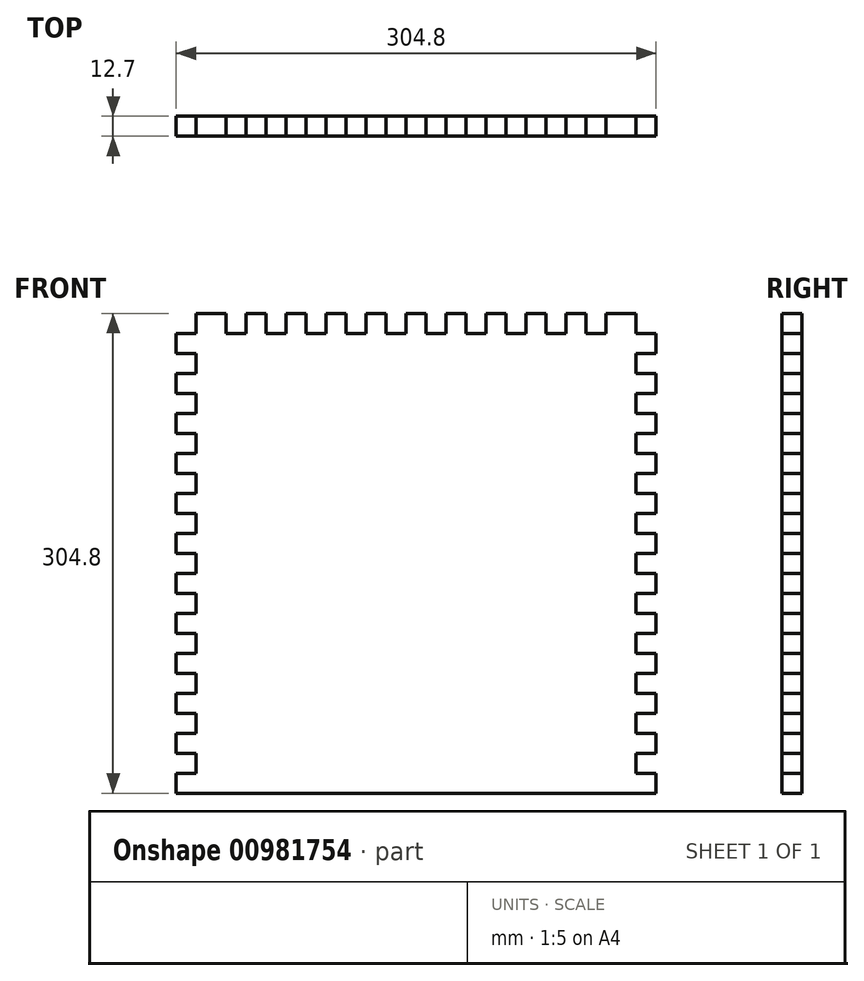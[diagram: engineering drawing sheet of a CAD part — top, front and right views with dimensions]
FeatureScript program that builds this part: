
annotation { "Feature Type Name" : "Feature", "Feature Type Description" : "" }
export const myFeature = defineFeature(function(context is Context, id is Id, definition is map)
    precondition{}
    {
        {
            var Q0;
            Q0=qCreatedBy(makeId("Front.planeOp"),FACE);
            var sketch = newSketch(context, id + "F0", { "sketchPlane" : qUnion([Q0])});
            skLineSegment(sketch, "E0.top", {"start": v(139.7, -142.06) * mm, "end": v(-139.7, -142.06) * mm});
            skPoint(sketch, "E0.middle", {"position": v(0, -2.36) * mm});
            skLineSegment(sketch, "E1", {"start": v(-139.7, -142.06) * mm, "end": v(-152.4, -142.06) * mm});
            skLineSegment(sketch, "E2", {"start": v(-152.4, -142.06) * mm, "end": v(-152.4, -129.36) * mm});
            skLineSegment(sketch, "E3", {"start": v(-152.4, -129.36) * mm, "end": v(-139.7, -129.36) * mm});
            skLineSegment(sketch, "E4", {"start": v(-139.7, -129.36) * mm, "end": v(-139.7, -116.66) * mm});
            skLineSegment(sketch, "E5.0.1.0", {"start": v(-152.4, -103.96) * mm, "end": v(-139.7, -103.96) * mm});
            skLineSegment(sketch, "E5.0.1.1", {"start": v(-139.7, -116.66) * mm, "end": v(-152.4, -116.66) * mm});
            skLineSegment(sketch, "E5.0.1.2", {"start": v(-152.4, -116.66) * mm, "end": v(-152.4, -103.96) * mm});
            skLineSegment(sketch, "E5.0.1.3", {"start": v(-139.7, -103.96) * mm, "end": v(-139.7, -91.26) * mm});
            skLineSegment(sketch, "E5.0.2.0", {"start": v(-152.4, -78.56) * mm, "end": v(-139.7, -78.56) * mm});
            skLineSegment(sketch, "E5.0.2.1", {"start": v(-139.7, -91.26) * mm, "end": v(-152.4, -91.26) * mm});
            skLineSegment(sketch, "E5.0.2.2", {"start": v(-152.4, -91.26) * mm, "end": v(-152.4, -78.56) * mm});
            skLineSegment(sketch, "E5.0.2.3", {"start": v(-139.7, -78.56) * mm, "end": v(-139.7, -65.86) * mm});
            skLineSegment(sketch, "E5.0.3.0", {"start": v(-152.4, -53.16) * mm, "end": v(-139.7, -53.16) * mm});
            skLineSegment(sketch, "E5.0.3.1", {"start": v(-139.7, -65.86) * mm, "end": v(-152.4, -65.86) * mm});
            skLineSegment(sketch, "E5.0.3.2", {"start": v(-152.4, -65.86) * mm, "end": v(-152.4, -53.16) * mm});
            skLineSegment(sketch, "E5.0.3.3", {"start": v(-139.7, -53.16) * mm, "end": v(-139.7, -40.46) * mm});
            skLineSegment(sketch, "E5.0.4.0", {"start": v(-152.4, -27.76) * mm, "end": v(-139.7, -27.76) * mm});
            skLineSegment(sketch, "E5.0.4.1", {"start": v(-139.7, -40.46) * mm, "end": v(-152.4, -40.46) * mm});
            skLineSegment(sketch, "E5.0.4.2", {"start": v(-152.4, -40.46) * mm, "end": v(-152.4, -27.76) * mm});
            skLineSegment(sketch, "E5.0.4.3", {"start": v(-139.7, -27.76) * mm, "end": v(-139.7, -15.06) * mm});
            skLineSegment(sketch, "E5.0.5.0", {"start": v(-152.4, -2.36) * mm, "end": v(-139.7, -2.36) * mm});
            skLineSegment(sketch, "E5.0.5.1", {"start": v(-139.7, -15.06) * mm, "end": v(-152.4, -15.06) * mm});
            skLineSegment(sketch, "E5.0.5.2", {"start": v(-152.4, -15.06) * mm, "end": v(-152.4, -2.36) * mm});
            skLineSegment(sketch, "E5.0.5.3", {"start": v(-139.7, -2.36) * mm, "end": v(-139.7, 10.34) * mm});
            skLineSegment(sketch, "E5.0.6.0", {"start": v(-152.4, 23.04) * mm, "end": v(-139.7, 23.04) * mm});
            skLineSegment(sketch, "E5.0.6.1", {"start": v(-139.7, 10.34) * mm, "end": v(-152.4, 10.34) * mm});
            skLineSegment(sketch, "E5.0.6.2", {"start": v(-152.4, 10.34) * mm, "end": v(-152.4, 23.04) * mm});
            skLineSegment(sketch, "E5.0.6.3", {"start": v(-139.7, 23.04) * mm, "end": v(-139.7, 35.74) * mm});
            skLineSegment(sketch, "E5.0.7.0", {"start": v(-152.4, 48.44) * mm, "end": v(-139.7, 48.44) * mm});
            skLineSegment(sketch, "E5.0.7.1", {"start": v(-139.7, 35.74) * mm, "end": v(-152.4, 35.74) * mm});
            skLineSegment(sketch, "E5.0.7.2", {"start": v(-152.4, 35.74) * mm, "end": v(-152.4, 48.44) * mm});
            skLineSegment(sketch, "E5.0.7.3", {"start": v(-139.7, 48.44) * mm, "end": v(-139.7, 61.14) * mm});
            skLineSegment(sketch, "E5.0.8.0", {"start": v(-152.4, 73.84) * mm, "end": v(-139.7, 73.84) * mm});
            skLineSegment(sketch, "E5.0.8.1", {"start": v(-139.7, 61.14) * mm, "end": v(-152.4, 61.14) * mm});
            skLineSegment(sketch, "E5.0.8.2", {"start": v(-152.4, 61.14) * mm, "end": v(-152.4, 73.84) * mm});
            skLineSegment(sketch, "E5.0.8.3", {"start": v(-139.7, 73.84) * mm, "end": v(-139.7, 86.54) * mm});
            skLineSegment(sketch, "E5.0.9.0", {"start": v(-152.4, 99.24) * mm, "end": v(-139.7, 99.24) * mm});
            skLineSegment(sketch, "E5.0.9.1", {"start": v(-139.7, 86.54) * mm, "end": v(-152.4, 86.54) * mm});
            skLineSegment(sketch, "E5.0.9.2", {"start": v(-152.4, 86.54) * mm, "end": v(-152.4, 99.24) * mm});
            skLineSegment(sketch, "E5.0.9.3", {"start": v(-139.7, 99.24) * mm, "end": v(-139.7, 111.94) * mm});
            skLineSegment(sketch, "E5.0.10.0", {"start": v(-152.4, 124.64) * mm, "end": v(-139.7, 124.64) * mm});
            skLineSegment(sketch, "E5.0.10.1", {"start": v(-139.7, 111.94) * mm, "end": v(-152.4, 111.94) * mm});
            skLineSegment(sketch, "E5.0.10.2", {"start": v(-152.4, 111.94) * mm, "end": v(-152.4, 124.64) * mm});
            skLineSegment(sketch, "E5.0.10.3", {"start": v(-139.7, 124.64) * mm, "end": v(-139.7, 137.34) * mm});
            skLineSegment(sketch, "E5.direction1", {"start": v(-152.4, -142.06) * mm, "end": v(-127, -142.06) * mm, "construction": true});
            skLineSegment(sketch, "E5.direction2", {"start": v(-152.4, -142.06) * mm, "end": v(-152.4, -116.66) * mm, "construction": true});
            skLineSegment(sketch, "E6.MirrorCS", {"start": v(139.7, 48.44) * mm, "end": v(139.7, 61.14) * mm});
            skLineSegment(sketch, "E7.MirrorCS", {"start": v(139.7, -27.76) * mm, "end": v(139.7, -15.06) * mm});
            skLineSegment(sketch, "E8.MirrorCS", {"start": v(152.4, 111.94) * mm, "end": v(152.4, 124.64) * mm});
            skLineSegment(sketch, "E9.MirrorCS", {"start": v(139.7, 124.64) * mm, "end": v(139.7, 137.34) * mm});
            skLineSegment(sketch, "E10.MirrorCS", {"start": v(139.7, -129.36) * mm, "end": v(139.7, -116.66) * mm});
            skLineSegment(sketch, "E11.MirrorCS", {"start": v(152.4, 10.34) * mm, "end": v(152.4, 23.04) * mm});
            skLineSegment(sketch, "E12.MirrorCS", {"start": v(139.7, -103.96) * mm, "end": v(139.7, -91.26) * mm});
            skLineSegment(sketch, "E13.MirrorCS", {"start": v(152.4, -15.06) * mm, "end": v(152.4, -2.36) * mm});
            skLineSegment(sketch, "E14.MirrorCS", {"start": v(152.4, -142.06) * mm, "end": v(152.4, -129.36) * mm});
            skLineSegment(sketch, "E15.MirrorCS", {"start": v(152.4, -91.26) * mm, "end": v(152.4, -78.56) * mm});
            skLineSegment(sketch, "E16.MirrorCS", {"start": v(152.4, -65.86) * mm, "end": v(152.4, -53.16) * mm});
            skLineSegment(sketch, "E17.MirrorCS", {"start": v(152.4, 35.74) * mm, "end": v(152.4, 48.44) * mm});
            skLineSegment(sketch, "E18.MirrorCS", {"start": v(139.7, 73.84) * mm, "end": v(139.7, 86.54) * mm});
            skLineSegment(sketch, "E19.MirrorCS", {"start": v(139.7, -53.16) * mm, "end": v(139.7, -40.46) * mm});
            skLineSegment(sketch, "E20.MirrorCS", {"start": v(152.4, 86.54) * mm, "end": v(152.4, 99.24) * mm});
            skLineSegment(sketch, "E21.MirrorCS", {"start": v(139.7, -116.66) * mm, "end": v(152.4, -116.66) * mm});
            skLineSegment(sketch, "E22.MirrorCS", {"start": v(152.4, 61.14) * mm, "end": v(152.4, 73.84) * mm});
            skLineSegment(sketch, "E23.MirrorCS", {"start": v(139.7, -78.56) * mm, "end": v(139.7, -65.86) * mm});
            skLineSegment(sketch, "E24.MirrorCS", {"start": v(152.4, 48.44) * mm, "end": v(139.7, 48.44) * mm});
            skLineSegment(sketch, "E25.MirrorCS", {"start": v(152.4, -53.16) * mm, "end": v(139.7, -53.16) * mm});
            skLineSegment(sketch, "E26.MirrorCS", {"start": v(139.7, 99.24) * mm, "end": v(139.7, 111.94) * mm});
            skLineSegment(sketch, "E27.MirrorCS", {"start": v(139.7, -142.06) * mm, "end": v(152.4, -142.06) * mm});
            skLineSegment(sketch, "E28.MirrorCS", {"start": v(152.4, -129.36) * mm, "end": v(139.7, -129.36) * mm});
            skLineSegment(sketch, "E29.MirrorCS", {"start": v(152.4, -78.56) * mm, "end": v(139.7, -78.56) * mm});
            skLineSegment(sketch, "E30.MirrorCS", {"start": v(139.7, -91.26) * mm, "end": v(152.4, -91.26) * mm});
            skLineSegment(sketch, "E31.MirrorCS", {"start": v(139.7, 10.34) * mm, "end": v(152.4, 10.34) * mm});
            skLineSegment(sketch, "E32.MirrorCS", {"start": v(139.7, 61.14) * mm, "end": v(152.4, 61.14) * mm});
            skLineSegment(sketch, "E33.MirrorCS", {"start": v(152.4, -27.76) * mm, "end": v(139.7, -27.76) * mm});
            skLineSegment(sketch, "E34.MirrorCS", {"start": v(152.4, 73.84) * mm, "end": v(139.7, 73.84) * mm});
            skLineSegment(sketch, "E35.MirrorCS", {"start": v(152.4, 99.24) * mm, "end": v(139.7, 99.24) * mm});
            skLineSegment(sketch, "E36.MirrorCS", {"start": v(152.4, -103.96) * mm, "end": v(139.7, -103.96) * mm});
            skLineSegment(sketch, "E37.MirrorCS", {"start": v(139.7, -65.86) * mm, "end": v(152.4, -65.86) * mm});
            skLineSegment(sketch, "E38.MirrorCS", {"start": v(152.4, 23.04) * mm, "end": v(139.7, 23.04) * mm});
            skLineSegment(sketch, "E39.MirrorCS", {"start": v(139.7, 35.74) * mm, "end": v(152.4, 35.74) * mm});
            skLineSegment(sketch, "E40.MirrorCS", {"start": v(139.7, -2.36) * mm, "end": v(139.7, 10.34) * mm});
            skLineSegment(sketch, "E41.MirrorCS", {"start": v(152.4, 124.64) * mm, "end": v(139.7, 124.64) * mm});
            skLineSegment(sketch, "E42.MirrorCS", {"start": v(139.7, -40.46) * mm, "end": v(152.4, -40.46) * mm});
            skLineSegment(sketch, "E43.MirrorCS", {"start": v(152.4, -116.66) * mm, "end": v(152.4, -103.96) * mm});
            skLineSegment(sketch, "E44.MirrorCS", {"start": v(139.7, -15.06) * mm, "end": v(152.4, -15.06) * mm});
            skLineSegment(sketch, "E45.MirrorCS", {"start": v(139.7, 111.94) * mm, "end": v(152.4, 111.94) * mm});
            skLineSegment(sketch, "E46.MirrorCS", {"start": v(139.7, 86.54) * mm, "end": v(152.4, 86.54) * mm});
            skLineSegment(sketch, "E47.MirrorCS", {"start": v(152.4, -40.46) * mm, "end": v(152.4, -27.76) * mm});
            skLineSegment(sketch, "E48.MirrorCS", {"start": v(139.7, 23.04) * mm, "end": v(139.7, 35.74) * mm});
            skLineSegment(sketch, "E49.MirrorCS", {"start": v(152.4, -2.36) * mm, "end": v(139.7, -2.36) * mm});
            skLineSegment(sketch, "E50.0.0.11", {"start": v(-152.4, 150.04) * mm, "end": v(-139.7, 150.04) * mm});
            skLineSegment(sketch, "E50.3.0.11", {"start": v(-139.7, 137.34) * mm, "end": v(-152.4, 137.34) * mm});
            skLineSegment(sketch, "E50.6.0.11", {"start": v(-152.4, 137.34) * mm, "end": v(-152.4, 150.04) * mm});
            skLineSegment(sketch, "E50.9.0.11", {"start": v(-139.7, 150.04) * mm, "end": v(-139.7, 162.74) * mm});
            skLineSegment(sketch, "E51", {"start": v(139.7, 137.34) * mm, "end": v(152.4, 137.34) * mm});
            skLineSegment(sketch, "E52", {"start": v(152.4, 137.34) * mm, "end": v(152.4, 150.04) * mm});
            skLineSegment(sketch, "E53", {"start": v(152.4, 150.04) * mm, "end": v(139.7, 150.04) * mm});
            skLineSegment(sketch, "E54", {"start": v(139.7, 150.04) * mm, "end": v(139.7, 162.74) * mm});
            skLineSegment(sketch, "E55", {"start": v(-139.7, 162.74) * mm, "end": v(-120.65, 162.74) * mm});
            skLineSegment(sketch, "E56", {"start": v(-120.65, 162.74) * mm, "end": v(-120.65, 150.04) * mm});
            skLineSegment(sketch, "E57", {"start": v(-120.65, 150.04) * mm, "end": v(-107.95, 150.04) * mm});
            skLineSegment(sketch, "E58", {"start": v(-107.95, 150.04) * mm, "end": v(-107.95, 162.74) * mm});
            skLineSegment(sketch, "E59", {"start": v(-107.95, 162.74) * mm, "end": v(-95.25, 162.74) * mm});
            skLineSegment(sketch, "E60.1.0.0", {"start": v(-82.55, 162.74) * mm, "end": v(-69.85, 162.74) * mm});
            skLineSegment(sketch, "E60.1.0.1", {"start": v(-95.25, 150.04) * mm, "end": v(-82.55, 150.04) * mm});
            skLineSegment(sketch, "E60.1.0.2", {"start": v(-82.55, 150.04) * mm, "end": v(-82.55, 162.74) * mm});
            skLineSegment(sketch, "E60.1.0.3", {"start": v(-95.25, 162.74) * mm, "end": v(-95.25, 150.04) * mm});
            skLineSegment(sketch, "E60.2.0.0", {"start": v(-57.15, 162.74) * mm, "end": v(-44.45, 162.74) * mm});
            skLineSegment(sketch, "E60.2.0.1", {"start": v(-69.85, 150.04) * mm, "end": v(-57.15, 150.04) * mm});
            skLineSegment(sketch, "E60.2.0.2", {"start": v(-57.15, 150.04) * mm, "end": v(-57.15, 162.74) * mm});
            skLineSegment(sketch, "E60.2.0.3", {"start": v(-69.85, 162.74) * mm, "end": v(-69.85, 150.04) * mm});
            skLineSegment(sketch, "E60.3.0.0", {"start": v(-31.75, 162.74) * mm, "end": v(-19.05, 162.74) * mm});
            skLineSegment(sketch, "E60.3.0.1", {"start": v(-44.45, 150.04) * mm, "end": v(-31.75, 150.04) * mm});
            skLineSegment(sketch, "E60.3.0.2", {"start": v(-31.75, 150.04) * mm, "end": v(-31.75, 162.74) * mm});
            skLineSegment(sketch, "E60.3.0.3", {"start": v(-44.45, 162.74) * mm, "end": v(-44.45, 150.04) * mm});
            skLineSegment(sketch, "E60.4.0.0", {"start": v(-6.35, 162.74) * mm, "end": v(6.35, 162.74) * mm});
            skLineSegment(sketch, "E60.4.0.1", {"start": v(-19.05, 150.04) * mm, "end": v(-6.35, 150.04) * mm});
            skLineSegment(sketch, "E60.4.0.2", {"start": v(-6.35, 150.04) * mm, "end": v(-6.35, 162.74) * mm});
            skLineSegment(sketch, "E60.4.0.3", {"start": v(-19.05, 162.74) * mm, "end": v(-19.05, 150.04) * mm});
            skLineSegment(sketch, "E60.5.0.0", {"start": v(19.05, 162.74) * mm, "end": v(31.75, 162.74) * mm});
            skLineSegment(sketch, "E60.5.0.1", {"start": v(6.35, 150.04) * mm, "end": v(19.05, 150.04) * mm});
            skLineSegment(sketch, "E60.5.0.2", {"start": v(19.05, 150.04) * mm, "end": v(19.05, 162.74) * mm});
            skLineSegment(sketch, "E60.5.0.3", {"start": v(6.35, 162.74) * mm, "end": v(6.35, 150.04) * mm});
            skLineSegment(sketch, "E60.6.0.0", {"start": v(44.45, 162.74) * mm, "end": v(57.15, 162.74) * mm});
            skLineSegment(sketch, "E60.6.0.1", {"start": v(31.75, 150.04) * mm, "end": v(44.45, 150.04) * mm});
            skLineSegment(sketch, "E60.6.0.2", {"start": v(44.45, 150.04) * mm, "end": v(44.45, 162.74) * mm});
            skLineSegment(sketch, "E60.6.0.3", {"start": v(31.75, 162.74) * mm, "end": v(31.75, 150.04) * mm});
            skLineSegment(sketch, "E60.7.0.0", {"start": v(69.85, 162.74) * mm, "end": v(82.55, 162.74) * mm});
            skLineSegment(sketch, "E60.7.0.1", {"start": v(57.15, 150.04) * mm, "end": v(69.85, 150.04) * mm});
            skLineSegment(sketch, "E60.7.0.2", {"start": v(69.85, 150.04) * mm, "end": v(69.85, 162.74) * mm});
            skLineSegment(sketch, "E60.7.0.3", {"start": v(57.15, 162.74) * mm, "end": v(57.15, 150.04) * mm});
            skLineSegment(sketch, "E60.8.0.0", {"start": v(95.25, 162.74) * mm, "end": v(107.95, 162.74) * mm});
            skLineSegment(sketch, "E60.8.0.1", {"start": v(82.55, 150.04) * mm, "end": v(95.25, 150.04) * mm});
            skLineSegment(sketch, "E60.8.0.2", {"start": v(95.25, 150.04) * mm, "end": v(95.25, 162.74) * mm});
            skLineSegment(sketch, "E60.8.0.3", {"start": v(82.55, 162.74) * mm, "end": v(82.55, 150.04) * mm});
            skLineSegment(sketch, "E60.9.0.1", {"start": v(107.95, 150.04) * mm, "end": v(120.65, 150.04) * mm});
            skLineSegment(sketch, "E60.9.0.2", {"start": v(120.65, 150.04) * mm, "end": v(120.65, 162.74) * mm});
            skLineSegment(sketch, "E60.9.0.3", {"start": v(107.95, 162.74) * mm, "end": v(107.95, 150.04) * mm});
            skLineSegment(sketch, "E61", {"start": v(120.65, 162.74) * mm, "end": v(139.7, 162.74) * mm});
            skSolve(sketch);
        }
        {
            var Q0;
            Q0=makeQuery(id+"F0.imprint","IMPRINT",FACE,{"disambiguationData":[TD([[makeQuery(id+"F0.imprint","IMPRINT",EDGE,{"derivedFrom":sQuery(id+"F0.wireOp",EDGE,"E0.top")}),-1.0]])]});
            extrude(context, id + "F1", {"entities" : qUnion([Q0]), "depth" : 12.7 * mm, "offsetDistance" : 25.4 * mm});
        }
    });
